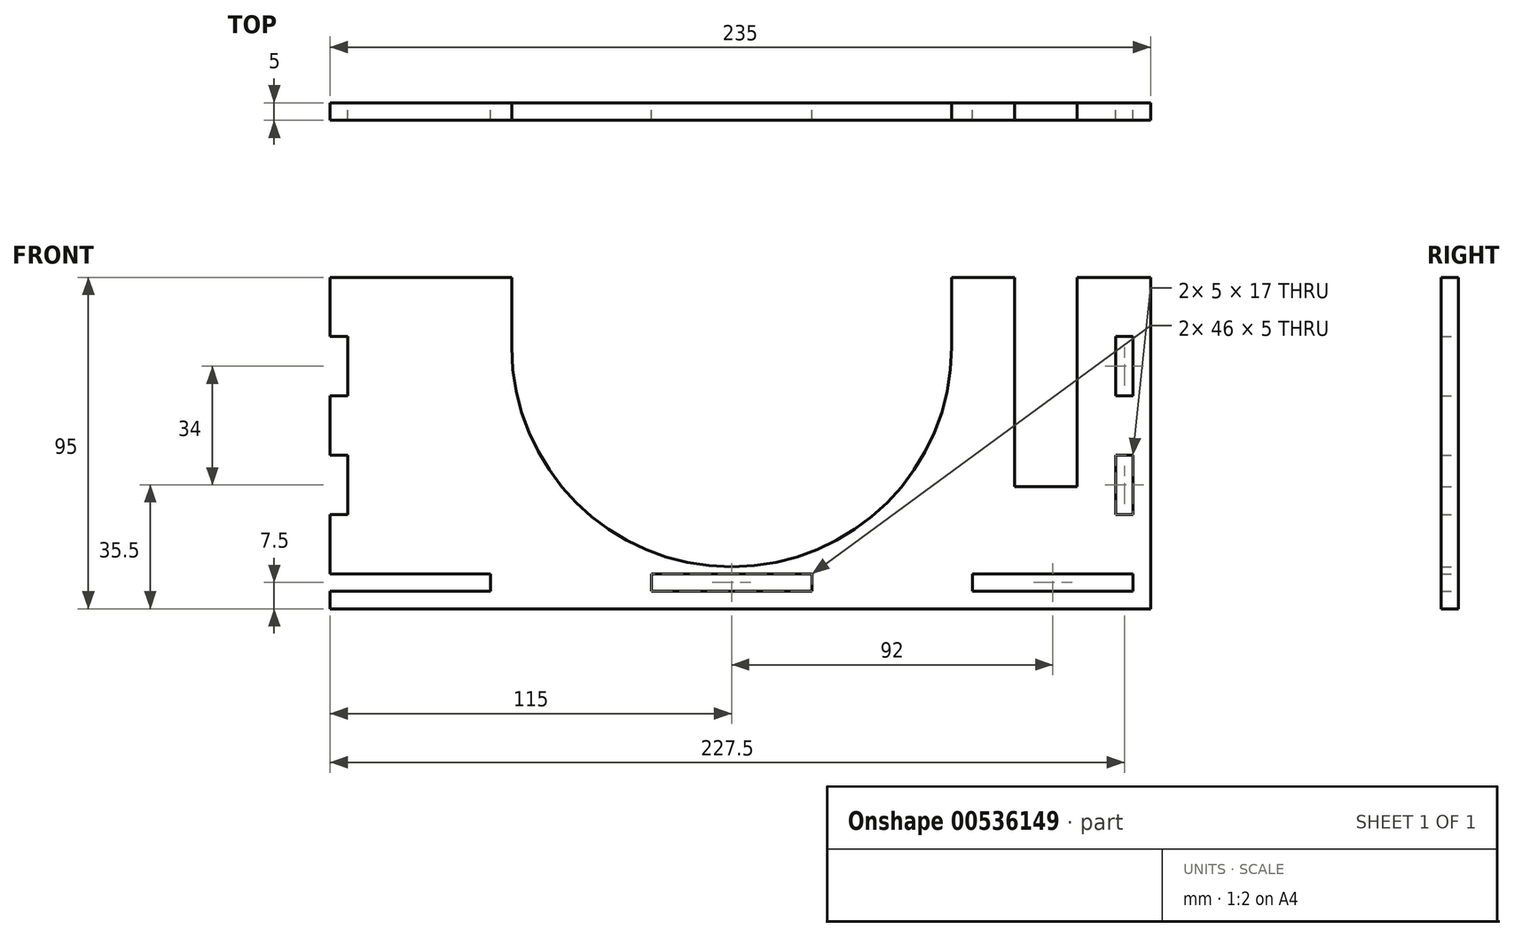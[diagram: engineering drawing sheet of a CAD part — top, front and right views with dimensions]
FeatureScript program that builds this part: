
annotation { "Feature Type Name" : "Feature", "Feature Type Description" : "" }
export const myFeature = defineFeature(function(context is Context, id is Id, definition is map)
    precondition{}
    {
        {
            var Q0;
            Q0=qCreatedBy(makeId("Front.planeOp"),FACE);
            var sketch = newSketch(context, id + "F0", { "sketchPlane" : qUnion([Q0])});
            skLineSegment(sketch, "E0.bottom", {"start": v(110, 42.5) * mm, "end": v(99, 42.5) * mm});
            skLineSegment(sketch, "E0.right", {"start": v(-110, 25.5) * mm, "end": v(-110, 8.5) * mm});
            skPoint(sketch, "E0.middle", {"position": v(0, 0) * mm});
            skLineSegment(sketch, "E1", {"start": v(-115, 42.5) * mm, "end": v(-115, -42.5) * mm, "construction": true});
            skLineSegment(sketch, "E2", {"start": v(115, -25.5) * mm, "end": v(115, -8.5) * mm, "construction": true});
            skArc(sketch, "E3", {"start": v(-63, 22.5) * mm, "mid": v(0, -40.5) * mm, "end": v(63, 22.5) * mm});
            skLineSegment(sketch, "E4.trimOffspring", {"start": v(-63, 42.5) * mm, "end": v(-110, 42.5) * mm});
            skLineSegment(sketch, "E5", {"start": v(-63, 22.5) * mm, "end": v(-63, 42.5) * mm});
            skLineSegment(sketch, "E6", {"start": v(63, 22.5) * mm, "end": v(63, 42.5) * mm});
            skLineSegment(sketch, "E7", {"start": v(-110, 42.5) * mm, "end": v(-115, 42.5) * mm});
            skLineSegment(sketch, "E8", {"start": v(-115, 25.5) * mm, "end": v(-110, 25.5) * mm});
            skLineSegment(sketch, "E9", {"start": v(-110, 8.5) * mm, "end": v(-115, 8.5) * mm});
            skLineSegment(sketch, "E10", {"start": v(-115, 8.5) * mm, "end": v(-115, -8.5) * mm});
            skLineSegment(sketch, "E11", {"start": v(-115, -8.5) * mm, "end": v(-110, -8.5) * mm});
            skLineSegment(sketch, "E12", {"start": v(-110, -8.5) * mm, "end": v(-110, -25.5) * mm});
            skLineSegment(sketch, "E13", {"start": v(-110, -25.5) * mm, "end": v(-115, -25.5) * mm});
            skLineSegment(sketch, "E14", {"start": v(-115, -25.5) * mm, "end": v(-115, -42.5) * mm});
            skLineSegment(sketch, "E15", {"start": v(-115, 42.5) * mm, "end": v(-115, 25.5) * mm});
            skLineSegment(sketch, "E16.MirrorCS", {"start": v(110, 42.5) * mm, "end": v(115, 42.5) * mm});
            skLineSegment(sketch, "E17.MirrorCS", {"start": v(115, -8.5) * mm, "end": v(110, -8.5) * mm});
            skLineSegment(sketch, "E18.MirrorCS", {"start": v(110, -25.5) * mm, "end": v(115, -25.5) * mm});
            skLineSegment(sketch, "E19.trimOffspring", {"start": v(110, -8.5) * mm, "end": v(110, -25.5) * mm});
            skLineSegment(sketch, "E20", {"start": v(-69, -42.5) * mm, "end": v(-69, -47.5) * mm});
            skLineSegment(sketch, "E21", {"start": v(-23, -42.5) * mm, "end": v(-23, -47.5) * mm});
            skLineSegment(sketch, "E22", {"start": v(23, -47.5) * mm, "end": v(23, -42.5) * mm});
            skLineSegment(sketch, "E23", {"start": v(69, -42.5) * mm, "end": v(69, -47.5) * mm});
            skLineSegment(sketch, "E24", {"start": v(69, -47.5) * mm, "end": v(115, -47.5) * mm});
            skPoint(sketch, "E25.end.orphan", {"position": v(-110, -42.5) * mm});
            skPoint(sketch, "E26.end.orphan", {"position": v(110, -42.5) * mm});
            skLineSegment(sketch, "E27", {"start": v(-115, -42.5) * mm, "end": v(-69, -42.5) * mm});
            skPoint(sketch, "E28.start.orphan", {"position": v(-115, -47.5) * mm});
            skLineSegment(sketch, "E29", {"start": v(-23, -42.5) * mm, "end": v(23, -42.5) * mm});
            skLineSegment(sketch, "E30.trimOffspring", {"start": v(69, -47.5) * mm, "end": v(115, -47.5) * mm, "construction": true});
            skLineSegment(sketch, "E31.bottom", {"start": v(-115, -47.5) * mm, "end": v(-69, -47.5) * mm});
            skLineSegment(sketch, "E31.top", {"start": v(-115, -52.5) * mm, "end": v(115, -52.5) * mm});
            skLineSegment(sketch, "E31.left", {"start": v(-115, -47.5) * mm, "end": v(-115, -52.5) * mm});
            skLineSegment(sketch, "E32", {"start": v(69, -42.5) * mm, "end": v(115, -42.5) * mm});
            skPoint(sketch, "E33.orphan", {"position": v(115, -47.5) * mm});
            skLineSegment(sketch, "E34", {"start": v(-23, -47.5) * mm, "end": v(23, -47.5) * mm});
            skLineSegment(sketch, "E35.bottom", {"start": v(115, 42.5) * mm, "end": v(120, 42.5) * mm});
            skLineSegment(sketch, "E35.top", {"start": v(115, -52.5) * mm, "end": v(120, -52.5) * mm});
            skLineSegment(sketch, "E35.right", {"start": v(120, 42.5) * mm, "end": v(120, -52.5) * mm});
            skPoint(sketch, "E36.orphan", {"position": v(115, 42.5) * mm});
            skLineSegment(sketch, "E37.trimOffspring", {"start": v(115, -8.5) * mm, "end": v(115, -25.5) * mm, "construction": true});
            skLineSegment(sketch, "E38.trimOffspring", {"start": v(115, -8.5) * mm, "end": v(115, -25.5) * mm});
            skLineSegment(sketch, "E39.trimOffspring", {"start": v(115, -42.5) * mm, "end": v(115, -47.5) * mm});
            skLineSegment(sketch, "E40.MirrorCS", {"start": v(115, 25.5) * mm, "end": v(110, 25.5) * mm});
            skLineSegment(sketch, "E41.MirrorCS", {"start": v(110, 25.5) * mm, "end": v(110, 8.5) * mm});
            skLineSegment(sketch, "E42.MirrorCS", {"start": v(110, 8.5) * mm, "end": v(115, 8.5) * mm});
            skLineSegment(sketch, "E43", {"start": v(115, 8.5) * mm, "end": v(115, 25.5) * mm});
            skLineSegment(sketch, "E44.top", {"start": v(81, -17.5) * mm, "end": v(99, -17.5) * mm});
            skLineSegment(sketch, "E44.left", {"start": v(81, 42.5) * mm, "end": v(81, -17.5) * mm});
            skLineSegment(sketch, "E44.right", {"start": v(99, 42.5) * mm, "end": v(99, -17.5) * mm});
            skLineSegment(sketch, "E45.trimOffspring", {"start": v(81, 42.5) * mm, "end": v(63, 42.5) * mm});
            skSolve(sketch);
        }
        {
            var Q0;
            Q0 = qSketchRegion(id + "F0", true);
            extrude(context, id + "F1", {"entities" : qUnion([Q0]), "depth" : 5 * mm, "offsetDistance" : 25 * mm});
        }
    });
